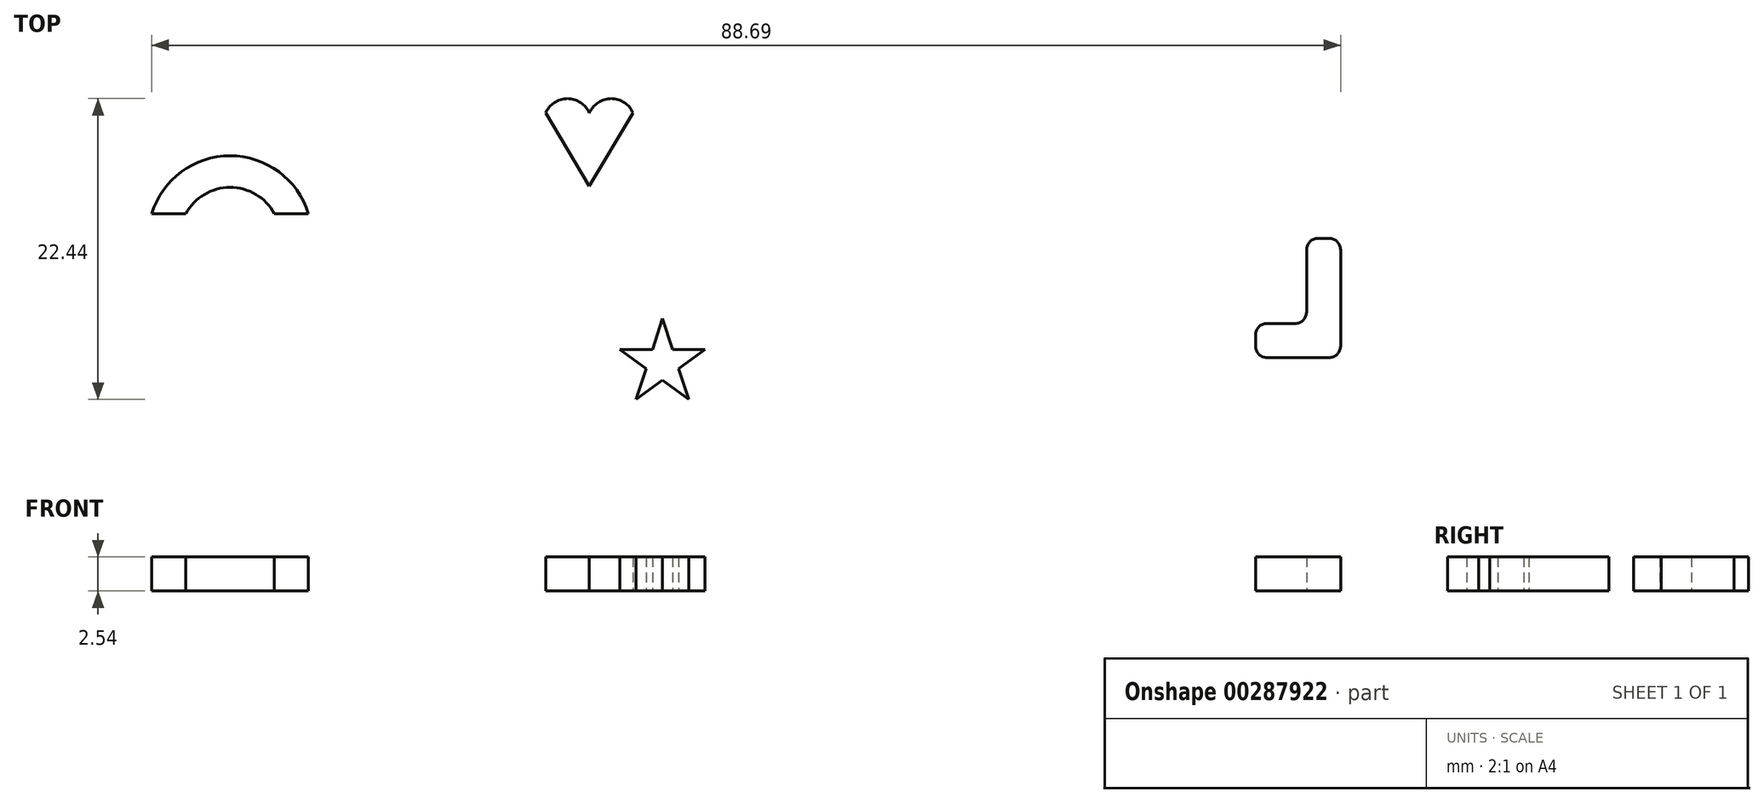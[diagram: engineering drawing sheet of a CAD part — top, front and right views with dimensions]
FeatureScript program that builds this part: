
annotation { "Feature Type Name" : "Feature", "Feature Type Description" : "" }
export const myFeature = defineFeature(function(context is Context, id is Id, definition is map)
    precondition{}
    {
        {
            var Q0;
            Q0=qCreatedBy(makeId("Top.planeOp"),FACE);
            var sketch = newSketch(context, id + "F0", { "sketchPlane" : qUnion([Q0])});
            skArc(sketch, "E0", {"start": v(-53.24, 37.54) * mm, "mid": v(-59.09, 41.85) * mm, "end": v(-64.93, 37.54) * mm});
            skArc(sketch, "E1", {"start": v(-55.78, 37.54) * mm, "mid": v(-59.09, 39.5) * mm, "end": v(-62.39, 37.54) * mm});
            skLineSegment(sketch, "E2", {"start": v(-64.93, 37.54) * mm, "end": v(-62.39, 37.54) * mm});
            skLineSegment(sketch, "E3", {"start": v(-55.78, 37.54) * mm, "end": v(-53.24, 37.54) * mm});
            skSolve(sketch);
        }
        {
            var Q0;
            Q0=makeQuery(id+"F0.imprint","IMPRINT",FACE,{"disambiguationData":[TD([[makeQuery(id+"F0.imprint","IMPRINT",EDGE,{"derivedFrom":sQuery(id+"F0.wireOp",EDGE,"E0")}),1.0]])]});
            extrude(context, id + "F1", {"entities" : qUnion([Q0]), "depth" : 2.54 * mm, "offsetDistance" : 25.4 * mm});
        }
        {
            var Q0;
            Q0=qCreatedBy(makeId("Top.planeOp"),FACE);
            var sketch = newSketch(context, id + "F2", { "sketchPlane" : qUnion([Q0])});
            skLineSegment(sketch, "E4", {"start": v(-28.8, 23.68) * mm, "end": v(-26.83, 29.72) * mm, "construction": true});
            skLineSegment(sketch, "E5", {"start": v(-26.83, 29.72) * mm, "end": v(-24.87, 23.68) * mm, "construction": true});
            skLineSegment(sketch, "E6", {"start": v(-24.87, 23.68) * mm, "end": v(-30, 27.41) * mm, "construction": true});
            skLineSegment(sketch, "E7", {"start": v(-30, 27.41) * mm, "end": v(-23.66, 27.41) * mm, "construction": true});
            skLineSegment(sketch, "E8", {"start": v(-23.66, 27.41) * mm, "end": v(-28.8, 23.68) * mm, "construction": true});
            skLineSegment(sketch, "E9", {"start": v(-27.58, 27.41) * mm, "end": v(-26.83, 29.72) * mm});
            skLineSegment(sketch, "E10", {"start": v(-26.83, 29.72) * mm, "end": v(-26.08, 27.41) * mm});
            skLineSegment(sketch, "E11", {"start": v(-26.08, 27.41) * mm, "end": v(-23.66, 27.41) * mm});
            skLineSegment(sketch, "E12", {"start": v(-25.62, 25.98) * mm, "end": v(-23.66, 27.41) * mm});
            skLineSegment(sketch, "E13", {"start": v(-25.62, 25.98) * mm, "end": v(-24.87, 23.68) * mm});
            skLineSegment(sketch, "E14", {"start": v(-24.87, 23.68) * mm, "end": v(-26.83, 25.1) * mm});
            skLineSegment(sketch, "E15", {"start": v(-26.83, 25.1) * mm, "end": v(-28.8, 23.68) * mm});
            skLineSegment(sketch, "E16", {"start": v(-28.04, 25.98) * mm, "end": v(-28.8, 23.68) * mm});
            skLineSegment(sketch, "E17", {"start": v(-28.04, 25.98) * mm, "end": v(-30, 27.41) * mm});
            skLineSegment(sketch, "E18", {"start": v(-30, 27.41) * mm, "end": v(-27.58, 27.41) * mm});
            skSolve(sketch);
        }
        {
            var Q0;
            Q0=makeQuery(id+"F2.imprint","IMPRINT",FACE,{"disambiguationData":[TD([[makeQuery(id+"F2.imprint","IMPRINT",EDGE,{"derivedFrom":sQuery(id+"F2.wireOp",EDGE,"E9")}),-1.0]])]});
            extrude(context, id + "F3", {"entities" : qUnion([Q0]), "depth" : 2.54 * mm, "offsetDistance" : 25.4 * mm});
        }
        {
            var Q0;
            Q0=qCreatedBy(makeId("Top.planeOp"),FACE);
            var sketch = newSketch(context, id + "F4", { "sketchPlane" : qUnion([Q0])});
            skLineSegment(sketch, "E19", {"start": v(-26.69, 45.04) * mm, "end": v(-45.6, 45.04) * mm, "construction": true});
            skLineSegment(sketch, "E20", {"start": v(-35.55, 45.04) * mm, "end": v(-32.28, 39.6) * mm});
            skLineSegment(sketch, "E21", {"start": v(-32.28, 39.6) * mm, "end": v(-29.02, 45.04) * mm});
            skPoint(sketch, "E22.visualSharp", {"position": v(-35.55, 45.04) * mm});
            skLineSegment(sketch, "E23", {"start": v(-32.28, 45.04) * mm, "end": v(-32.28, 36.61) * mm, "construction": true});
            skLineSegment(sketch, "E24", {"start": v(-36.3, 44.35) * mm, "end": v(-27.97, 44.35) * mm, "construction": true});
            skArc(sketch, "E25", {"start": v(-32.28, 45.04) * mm, "mid": v(-33.91, 46.12) * mm, "end": v(-35.55, 45.04) * mm});
            skArc(sketch, "E26", {"start": v(-29.02, 45.04) * mm, "mid": v(-30.65, 46.12) * mm, "end": v(-32.28, 45.04) * mm});
            skSolve(sketch);
        }
        {
            var Q0;
            Q0=qCreatedBy(makeId("Top.planeOp"),FACE);
            var sketch = newSketch(context, id + "F5", { "sketchPlane" : qUnion([Q0])});
            skLineSegment(sketch, "E27", {"start": v(18.4, 26.8) * mm, "end": v(23.76, 26.8) * mm});
            skLineSegment(sketch, "E28", {"start": v(23.76, 26.8) * mm, "end": v(23.76, 35.7) * mm});
            skLineSegment(sketch, "E29", {"start": v(23.76, 35.7) * mm, "end": v(21.22, 35.7) * mm});
            skLineSegment(sketch, "E30", {"start": v(21.22, 35.7) * mm, "end": v(21.22, 29.34) * mm});
            skLineSegment(sketch, "E31", {"start": v(21.22, 29.34) * mm, "end": v(17.4, 29.34) * mm});
            skLineSegment(sketch, "E32", {"start": v(17.4, 29.34) * mm, "end": v(17.4, 26.8) * mm});
            skLineSegment(sketch, "E33", {"start": v(17.4, 26.8) * mm, "end": v(18.4, 26.8) * mm});
            skSolve(sketch);
        }
        {
            var Q0;
            Q0=makeQuery(id+"F5.imprint","IMPRINT",FACE,{"disambiguationData":[TD([[makeQuery(id+"F5.imprint","IMPRINT",EDGE,{"derivedFrom":sQuery(id+"F5.wireOp",EDGE,"E27")}),1.0]])]});
            extrude(context, id + "F6", {"entities" : qUnion([Q0]), "depth" : 2.54 * mm, "offsetDistance" : 25.4 * mm});
        }
        {
            var Q0;
            Q0=makeQuery(id+"F6.opExtrude","SWEPT_EDGE",EDGE,{"disambiguationData":[OSD([sQuery(id+"F5.wireOp",EDGE,"E31"),sQuery(id+"F5.wireOp",EDGE,"E32")])]});
            var Q1;
            Q1=makeQuery(id+"F6.opExtrude","SWEPT_EDGE",EDGE,{"disambiguationData":[OSD([sQuery(id+"F5.wireOp",EDGE,"E30"),sQuery(id+"F5.wireOp",EDGE,"E31")])]});
            var Q2;
            Q2=makeQuery(id+"F6.opExtrude","SWEPT_EDGE",EDGE,{"disambiguationData":[OSD([sQuery(id+"F5.wireOp",EDGE,"E32"),sQuery(id+"F5.wireOp",EDGE,"E33")])]});
            var Q3;
            Q3=makeQuery(id+"F6.opExtrude","SWEPT_EDGE",EDGE,{"disambiguationData":[OSD([sQuery(id+"F5.wireOp",EDGE,"E27"),sQuery(id+"F5.wireOp",EDGE,"E28")])]});
            var Q4;
            Q4=makeQuery(id+"F6.opExtrude","SWEPT_EDGE",EDGE,{"disambiguationData":[OSD([sQuery(id+"F5.wireOp",EDGE,"E28"),sQuery(id+"F5.wireOp",EDGE,"E29")])]});
            var Q5;
            Q5=makeQuery(id+"F6.opExtrude","SWEPT_EDGE",EDGE,{"disambiguationData":[OSD([sQuery(id+"F5.wireOp",EDGE,"E29"),sQuery(id+"F5.wireOp",EDGE,"E30")])]});
            fillet(context, id + "F7", {"entities" : qUnion([Q0, Q1, Q2, Q3, Q4, Q5]), "radius" : 0.86 * mm, "tangentPropagation" : true, "allowEdgeOverflow" : false});
        }
        {
            var Q0;
            Q0=makeQuery(id+"F4.imprint","IMPRINT",FACE,{"disambiguationData":[TD([[makeQuery(id+"F4.imprint","IMPRINT",EDGE,{"derivedFrom":sQuery(id+"F4.wireOp",EDGE,"E20")}),1.0]])]});
            extrude(context, id + "F8", {"entities" : qUnion([Q0]), "depth" : 2.54 * mm, "offsetDistance" : 25.4 * mm});
        }
    });
